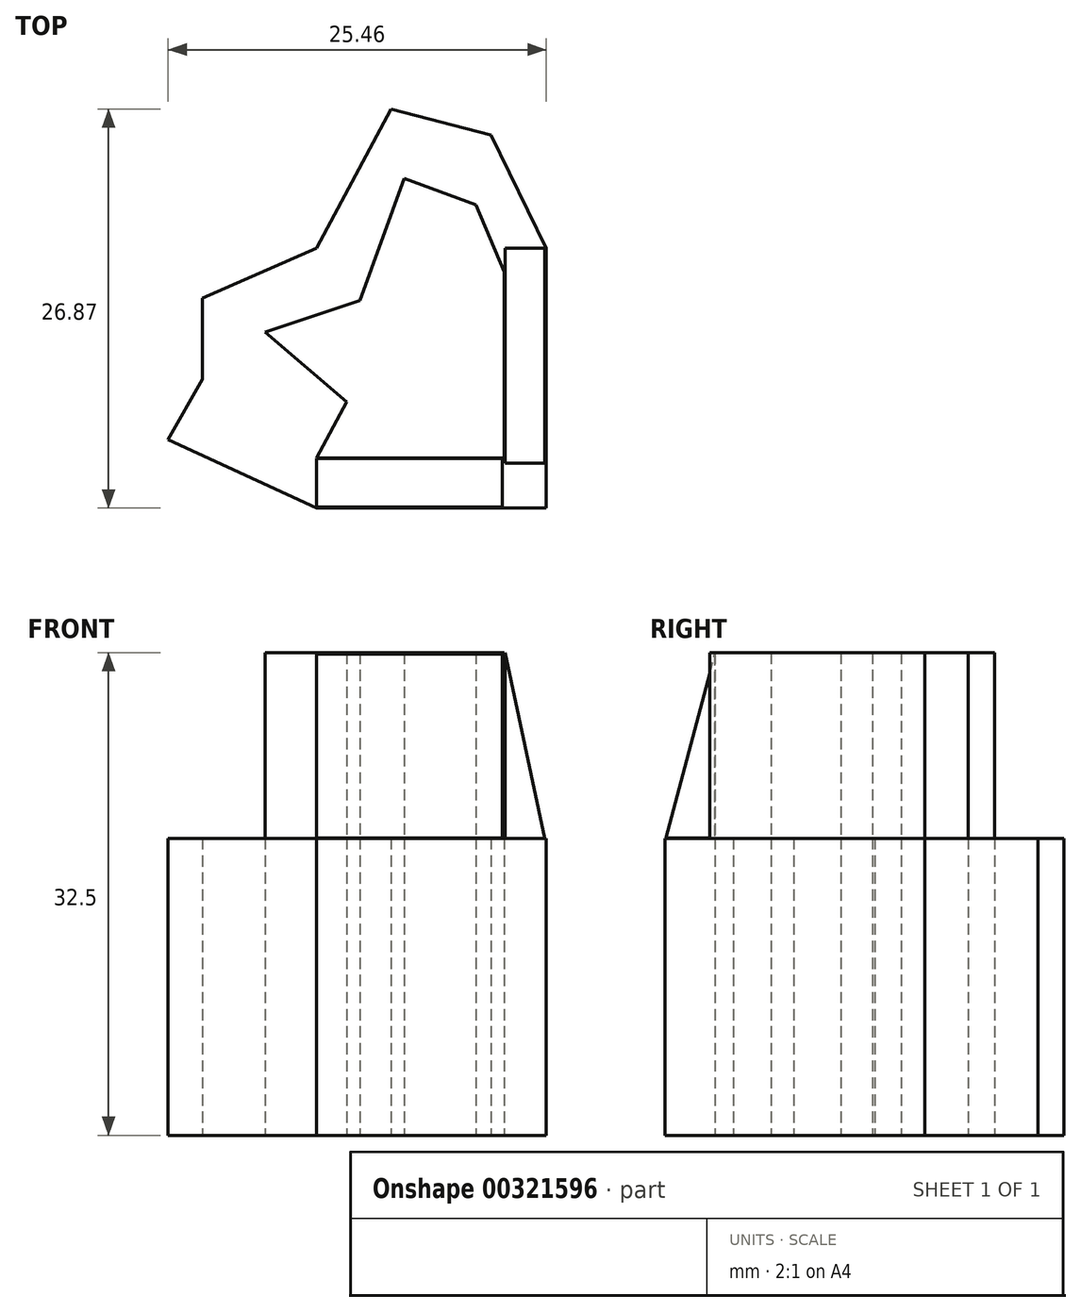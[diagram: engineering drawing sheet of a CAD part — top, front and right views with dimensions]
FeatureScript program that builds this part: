
annotation { "Feature Type Name" : "Feature", "Feature Type Description" : "" }
export const myFeature = defineFeature(function(context is Context, id is Id, definition is map)
    precondition{}
    {
        {
            var Q0;
            Q0=qCreatedBy(makeId("Top.planeOp"),FACE);
            var sketch = newSketch(context, id + "F0", { "sketchPlane" : qUnion([Q0])});
            skLineSegment(sketch, "E0.bottom", {"start": v(0, 0) * mm, "end": v(15.47, 0) * mm});
            skLineSegment(sketch, "E0.top", {"start": v(0, -17.5) * mm, "end": v(15.47, -17.5) * mm});
            skLineSegment(sketch, "E0.right", {"start": v(15.47, 0) * mm, "end": v(15.47, -17.5) * mm});
            skLineSegment(sketch, "E1", {"start": v(0, 0) * mm, "end": v(5.04, 9.37) * mm});
            skLineSegment(sketch, "E2", {"start": v(5.04, 9.37) * mm, "end": v(11.76, 7.6) * mm});
            skLineSegment(sketch, "E3", {"start": v(11.76, 7.6) * mm, "end": v(15.47, 0) * mm});
            skLineSegment(sketch, "E4", {"start": v(0, 0) * mm, "end": v(-7.69, -3.36) * mm});
            skLineSegment(sketch, "E5", {"start": v(-7.69, -3.36) * mm, "end": v(-7.69, -8.84) * mm});
            skLineSegment(sketch, "E6", {"start": v(-7.69, -8.84) * mm, "end": v(-9.99, -12.9) * mm});
            skLineSegment(sketch, "E7", {"start": v(-9.99, -12.9) * mm, "end": v(0, -17.5) * mm});
            skLineSegment(sketch, "E8", {"start": v(-3.45, -5.66) * mm, "end": v(2.92, -3.54) * mm});
            skLineSegment(sketch, "E9", {"start": v(2.92, -3.54) * mm, "end": v(5.92, 4.68) * mm});
            skPoint(sketch, "E9.endSnap0", {"position": v(2.52, 4.68) * mm});
            skLineSegment(sketch, "E10", {"start": v(5.92, 4.68) * mm, "end": v(10.73, 2.93) * mm});
            skLineSegment(sketch, "E11", {"start": v(10.73, 2.93) * mm, "end": v(12.64, -1.6) * mm});
            skLineSegment(sketch, "E12", {"start": v(12.64, -1.6) * mm, "end": v(12.64, -14.14) * mm});
            skLineSegment(sketch, "E13", {"start": v(12.64, -14.14) * mm, "end": v(0, -14.14) * mm});
            skLineSegment(sketch, "E14", {"start": v(0, -14.14) * mm, "end": v(2.04, -10.35) * mm});
            skLineSegment(sketch, "E15", {"start": v(2.04, -10.35) * mm, "end": v(-3.45, -5.66) * mm});
            skSolve(sketch);
        }
        {
            var Q0;
            Q0=makeQuery(id+"F0.imprint","IMPRINT",FACE,{"disambiguationData":[TD([[makeQuery(id+"F0.imprint","IMPRINT",EDGE,{"derivedFrom":sQuery(id+"F0.wireOp",EDGE,"E0.bottom")}),-1.0]])]});
            var Q1;
            Q1=makeQuery(id+"F0.imprint","IMPRINT",FACE,{"disambiguationData":[TD([[makeQuery(id+"F0.imprint","IMPRINT",EDGE,{"derivedFrom":sQuery(id+"F0.wireOp",EDGE,"E0.bottom")}),1.0]])]});
            extrude(context, id + "F1", {"entities" : qUnion([Q0, Q1]), "depth" : 20 * mm});
        }
        {
            var Q0;
            Q0=makeQuery(id+"F1.opExtrude","CAP_FACE",FACE,{"disambiguationData":[OSD([sQuery(id+"F0.wireOp",EDGE,"E0.top"),sQuery(id+"F0.wireOp",EDGE,"E0.right"),sQuery(id+"F0.wireOp",EDGE,"E1"),sQuery(id+"F0.wireOp",EDGE,"E2"),sQuery(id+"F0.wireOp",EDGE,"E3"),sQuery(id+"F0.wireOp",EDGE,"E4"),sQuery(id+"F0.wireOp",EDGE,"E5"),sQuery(id+"F0.wireOp",EDGE,"E6"),sQuery(id+"F0.wireOp",EDGE,"E7"),sQuery(id+"F0.wireOp",EDGE,"E8"),sQuery(id+"F0.wireOp",EDGE,"E9"),sQuery(id+"F0.wireOp",EDGE,"E10"),sQuery(id+"F0.wireOp",EDGE,"E11"),sQuery(id+"F0.wireOp",EDGE,"E12"),sQuery(id+"F0.wireOp",EDGE,"E13"),sQuery(id+"F0.wireOp",EDGE,"E14"),sQuery(id+"F0.wireOp",EDGE,"E15")])],"isStart":false});
            var sketch = newSketch(context, id + "F2", { "sketchPlane" : qUnion([Q0])});
            skLineSegment(sketch, "E16", {"start": v(-3.45, -5.66) * mm, "end": v(2.04, -10.35) * mm});
            skLineSegment(sketch, "E17", {"start": v(2.04, -10.35) * mm, "end": v(0, -14.14) * mm});
            skLineSegment(sketch, "E18", {"start": v(0, -14.14) * mm, "end": v(12.64, -14.14) * mm});
            skLineSegment(sketch, "E19", {"start": v(12.64, -14.14) * mm, "end": v(12.64, -1.6) * mm});
            skLineSegment(sketch, "E20", {"start": v(12.64, -1.6) * mm, "end": v(10.73, 2.93) * mm});
            skLineSegment(sketch, "E21", {"start": v(10.73, 2.93) * mm, "end": v(5.92, 4.68) * mm});
            skLineSegment(sketch, "E22", {"start": v(5.92, 4.68) * mm, "end": v(2.92, -3.54) * mm});
            skLineSegment(sketch, "E23", {"start": v(2.92, -3.54) * mm, "end": v(-3.45, -5.66) * mm});
            skSolve(sketch);
        }
        {
            var Q0;
            Q0=makeQuery(id+"F2.imprint","IMPRINT",FACE,{"disambiguationData":[TD([[makeQuery(id+"F2.imprint","IMPRINT",EDGE,{"derivedFrom":sQuery(id+"F2.wireOp",EDGE,"E16")}),-1.0]])]});
            extrude(context, id + "F3", {"entities" : qUnion([Q0]), "depth" : 12.5 * mm});
        }
        {
            var Q0;
            Q0=qCreatedBy(makeId("Right.planeOp"),FACE);
            var sketch = newSketch(context, id + "F4", { "sketchPlane" : qUnion([Q0])});
            skLineSegment(sketch, "E24", {"start": v(-14.15, 32.4) * mm, "end": v(-14.15, 20.02) * mm});
            skLineSegment(sketch, "E25", {"start": v(-14.15, 20.02) * mm, "end": v(-17.45, 20.02) * mm});
            skLineSegment(sketch, "E26", {"start": v(-17.45, 20.02) * mm, "end": v(-14.15, 32.4) * mm});
            skSolve(sketch);
        }
        {
            var Q0;
            Q0=makeQuery(id+"F4.imprint","IMPRINT",FACE,{"disambiguationData":[TD([[makeQuery(id+"F4.imprint","IMPRINT",EDGE,{"derivedFrom":sQuery(id+"F4.wireOp",EDGE,"E24")}),-1.0]])]});
            extrude(context, id + "F5", {"entities" : qUnion([Q0]), "depth" : 12.5 * mm});
        }
        {
            var Q0;
            Q0=qCreatedBy(makeId("Front.planeOp"),FACE);
            var sketch = newSketch(context, id + "F6", { "sketchPlane" : qUnion([Q0])});
            skLineSegment(sketch, "E27", {"start": v(15.37, 19.99) * mm, "end": v(12.7, 19.99) * mm});
            skLineSegment(sketch, "E28", {"start": v(12.7, 19.99) * mm, "end": v(12.7, 32.49) * mm});
            skLineSegment(sketch, "E29", {"start": v(12.7, 32.49) * mm, "end": v(15.37, 19.99) * mm});
            skSolve(sketch);
        }
        {
            var Q0;
            Q0=makeQuery(id+"F6.imprint","IMPRINT",FACE,{"disambiguationData":[TD([[makeQuery(id+"F6.imprint","IMPRINT",EDGE,{"derivedFrom":sQuery(id+"F6.wireOp",EDGE,"E27")}),-1.0]])]});
            extrude(context, id + "F7", {"entities" : qUnion([Q0]), "operationType" : NewBodyOperationType.ADD, "depth" : 14.5 * mm});
        }
    });
